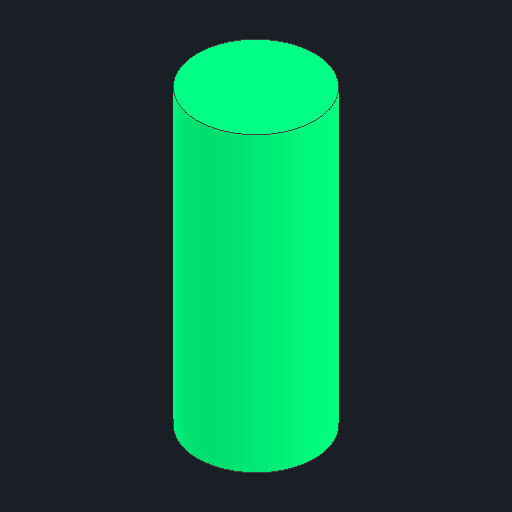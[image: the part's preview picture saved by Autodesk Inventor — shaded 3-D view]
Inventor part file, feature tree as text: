
AUTODESK INVENTOR PART (.ipt)
format: ipt  version: 2025.2 (Build 292293000, 293)  size: 231,424 bytes
history: native  units: mm
features: extrude x1, sketch x1
ambient origin geometry x8: Origin, YZ Plane, XZ Plane, XY Plane, X Axis, Y Axis, Z Axis, Center Point
bodies: Solid1 (feature_tree)
feature tree (2):
  extrude  "Extrusion1"  Depth=65.0mm TaperAngle=0.0deg
  sketch  "Sketch1"  dims[d0=26.0mm d1=65.0mm d2=0.0mm]
